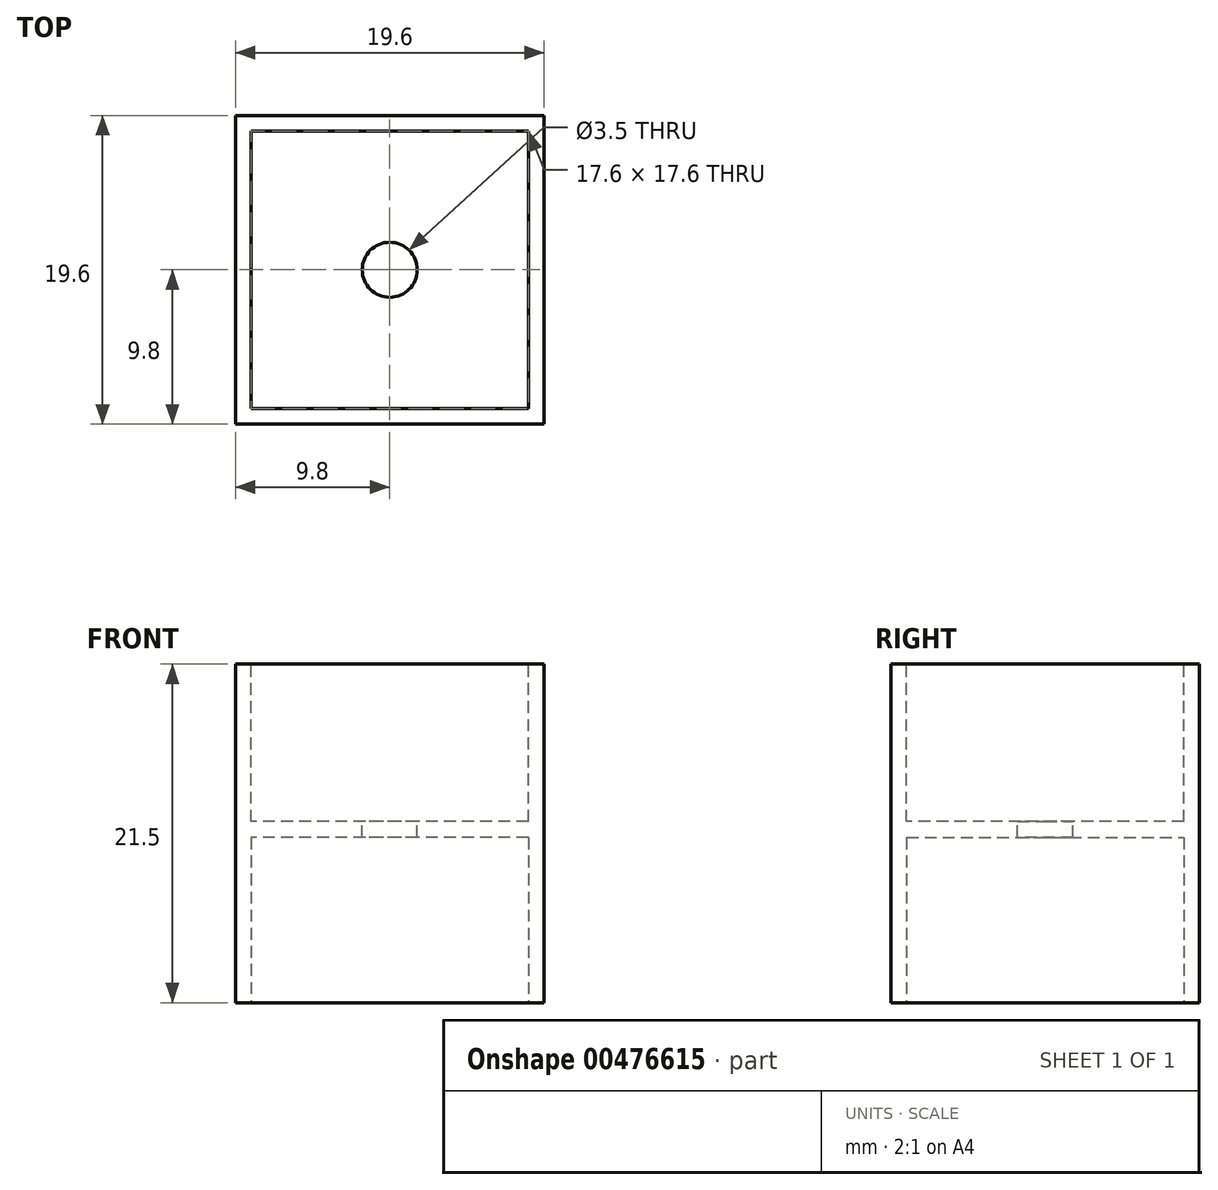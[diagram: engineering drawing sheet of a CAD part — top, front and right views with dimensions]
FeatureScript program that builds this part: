
annotation { "Feature Type Name" : "Feature", "Feature Type Description" : "" }
export const myFeature = defineFeature(function(context is Context, id is Id, definition is map)
    precondition{}
    {
        {
            var Q0;
            Q0=qCreatedBy(makeId("Top.planeOp"),FACE);
            var sketch = newSketch(context, id + "F0", { "sketchPlane" : qUnion([Q0])});
            skLineSegment(sketch, "E0.bottom", {"start": v(9.8, 9.8) * mm, "end": v(-9.8, 9.8) * mm});
            skLineSegment(sketch, "E0.top", {"start": v(9.8, -9.8) * mm, "end": v(-9.8, -9.8) * mm});
            skLineSegment(sketch, "E0.left", {"start": v(9.8, 9.8) * mm, "end": v(9.8, -9.8) * mm});
            skLineSegment(sketch, "E0.right", {"start": v(-9.8, 9.8) * mm, "end": v(-9.8, -9.8) * mm});
            skPoint(sketch, "E0.middle", {"position": v(0, 0) * mm});
            skSolve(sketch);
        }
        {
            var Q0;
            Q0=makeQuery(id+"F0.imprint","IMPRINT",FACE,{"disambiguationData":[TD([[makeQuery(id+"F0.imprint","IMPRINT",EDGE,{"derivedFrom":sQuery(id+"F0.wireOp",EDGE,"E0.bottom")}),1.0]])]});
            extrude(context, id + "F1", {"entities" : qUnion([Q0]), "depth" : 21.5 * mm, "offsetDistance" : 25 * mm});
        }
        {
            var Q0;
            Q0=makeQuery(id+"F1.opExtrude","CAP_FACE",FACE,{"disambiguationData":[OSD([sQuery(id+"F0.wireOp",EDGE,"E0.bottom"),sQuery(id+"F0.wireOp",EDGE,"E0.top"),sQuery(id+"F0.wireOp",EDGE,"E0.left"),sQuery(id+"F0.wireOp",EDGE,"E0.right")])],"isStart":true});
            var sketch = newSketch(context, id + "F2", { "sketchPlane" : qUnion([Q0])});
            skLineSegment(sketch, "E1.bottom", {"start": v(8.8, 8.8) * mm, "end": v(-8.8, 8.8) * mm});
            skLineSegment(sketch, "E1.top", {"start": v(8.8, -8.8) * mm, "end": v(-8.8, -8.8) * mm});
            skLineSegment(sketch, "E1.left", {"start": v(8.8, 8.8) * mm, "end": v(8.8, -8.8) * mm});
            skLineSegment(sketch, "E1.right", {"start": v(-8.8, 8.8) * mm, "end": v(-8.8, -8.8) * mm});
            skPoint(sketch, "E1.middle", {"position": v(0, 0) * mm});
            skSolve(sketch);
        }
        {
            var Q0;
            Q0 = qSketchRegion(id + "F2", true);
            extrude(context, id + "F3", {"entities" : qUnion([Q0]), "operationType" : NewBodyOperationType.REMOVE, "oppositeDirection" : true, "depth" : 10.5 * mm, "offsetDistance" : 25 * mm});
        }
        {
            var Q0;
            Q0=makeQuery(id+"F1.opExtrude","CAP_FACE",FACE,{"disambiguationData":[OSD([sQuery(id+"F0.wireOp",EDGE,"E0.bottom"),sQuery(id+"F0.wireOp",EDGE,"E0.top"),sQuery(id+"F0.wireOp",EDGE,"E0.left"),sQuery(id+"F0.wireOp",EDGE,"E0.right")])],"isStart":false});
            var sketch = newSketch(context, id + "F4", { "sketchPlane" : qUnion([Q0])});
            skLineSegment(sketch, "E2.bottom", {"start": v(8.8, 8.8) * mm, "end": v(-8.8, 8.8) * mm});
            skLineSegment(sketch, "E2.top", {"start": v(8.8, -8.8) * mm, "end": v(-8.8, -8.8) * mm});
            skLineSegment(sketch, "E2.left", {"start": v(8.8, 8.8) * mm, "end": v(8.8, -8.8) * mm});
            skLineSegment(sketch, "E2.right", {"start": v(-8.8, 8.8) * mm, "end": v(-8.8, -8.8) * mm});
            skPoint(sketch, "E2.middle", {"position": v(0, 0) * mm});
            skSolve(sketch);
        }
        {
            var Q0;
            Q0 = qSketchRegion(id + "F4", true);
            extrude(context, id + "F5", {"entities" : qUnion([Q0]), "operationType" : NewBodyOperationType.REMOVE, "oppositeDirection" : true, "depth" : 10 * mm, "offsetDistance" : 25 * mm});
        }
        {
            var Q0;
            Q0=makeQuery(id+"F5.boolean.opBoolean","COPY",FACE,{"derivedFrom":makeQuery(id+"F5.opExtrude","CAP_FACE",FACE,{"disambiguationData":[OSD([sQuery(id+"F4.wireOp",EDGE,"E2.bottom"),sQuery(id+"F4.wireOp",EDGE,"E2.top"),sQuery(id+"F4.wireOp",EDGE,"E2.left"),sQuery(id+"F4.wireOp",EDGE,"E2.right")])],"isStart":false})});
            var sketch = newSketch(context, id + "F6", { "sketchPlane" : qUnion([Q0])});
            skCircle(sketch, "E3", {"center": v(0, 0) * mm, "radius": 1.75 * mm});
            skSolve(sketch);
        }
        {
            var Q0;
            Q0 = qSketchRegion(id + "F6", true);
            extrude(context, id + "F7", {"entities" : qUnion([Q0]), "operationType" : NewBodyOperationType.REMOVE, "oppositeDirection" : true, "depth" : 1 * mm, "offsetDistance" : 25 * mm});
        }
    });
